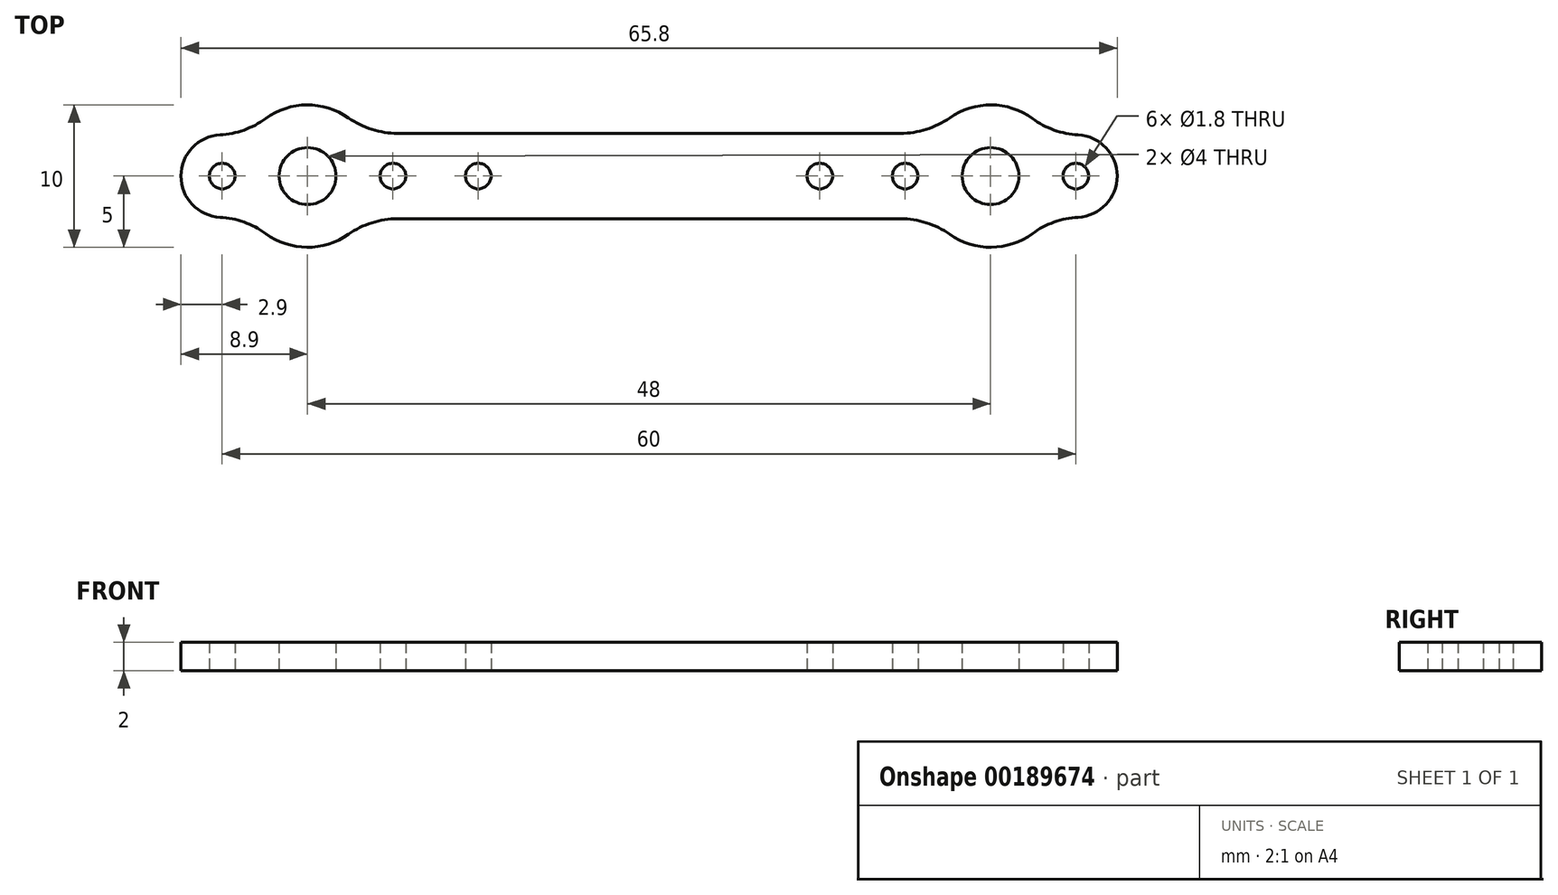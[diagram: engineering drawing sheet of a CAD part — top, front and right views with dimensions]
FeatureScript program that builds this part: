
annotation { "Feature Type Name" : "Feature", "Feature Type Description" : "" }
export const myFeature = defineFeature(function(context is Context, id is Id, definition is map)
    precondition{}
    {
        {
            var Q0;
            Q0=qCreatedBy(makeId("Top.planeOp"),FACE);
            var sketch = newSketch(context, id + "F0", { "sketchPlane" : qUnion([Q0])});
            skLineSegment(sketch, "E0", {"start": v(-24, 0) * mm, "end": v(0, 0) * mm, "construction": true});
            skCircle(sketch, "E1", {"center": v(-24, 0) * mm, "radius": 2 * mm});
            skCircle(sketch, "E2", {"center": v(-18, 0) * mm, "radius": 0.9 * mm});
            skCircle(sketch, "E3", {"center": v(-12, 0) * mm, "radius": 0.9 * mm});
            skCircle(sketch, "E4", {"center": v(-30, 0) * mm, "radius": 0.9 * mm});
            skLineSegment(sketch, "E5", {"start": v(0, 3) * mm, "end": v(-17.68, 3) * mm});
            skLineSegment(sketch, "E6.MirrorCS", {"start": v(0, -3) * mm, "end": v(-17.68, -3) * mm});
            skArc(sketch, "E7.0", {"start": v(-26.95, -4.04) * mm, "mid": v(-24.04, -5) * mm, "end": v(-21.13, -4.1) * mm});
            skArc(sketch, "E8.0", {"start": v(-30.16, 2.9) * mm, "mid": v(-32.9, 0) * mm, "end": v(-30.16, -2.9) * mm});
            skArc(sketch, "E9.trimOffspring", {"start": v(-21.13, 4.1) * mm, "mid": v(-24.04, 5) * mm, "end": v(-26.95, 4.04) * mm});
            skPoint(sketch, "E10.visualSharp", {"position": v(-20, 3) * mm});
            skArc(sketch, "E10.filletArc", {"start": v(-21.13, 4.1) * mm, "mid": v(-19.48, 3.28) * mm, "end": v(-17.68, 3) * mm});
            skPoint(sketch, "E11.visualSharp", {"position": v(-20, -3) * mm});
            skArc(sketch, "E11.filletArc", {"start": v(-17.68, -3) * mm, "mid": v(-19.48, -3.28) * mm, "end": v(-21.13, -4.1) * mm});
            skPoint(sketch, "E12.visualSharp", {"position": v(-28.38, 2.4) * mm});
            skArc(sketch, "E12.filletArc", {"start": v(-30.16, 2.9) * mm, "mid": v(-28.47, 3.23) * mm, "end": v(-26.95, 4.04) * mm});
            skPoint(sketch, "E13.visualSharp", {"position": v(-28.38, -2.4) * mm});
            skArc(sketch, "E13.filletArc", {"start": v(-26.95, -4.04) * mm, "mid": v(-28.47, -3.23) * mm, "end": v(-30.16, -2.9) * mm});
            skLineSegment(sketch, "E14", {"start": v(0, 9.05) * mm, "end": v(0, -10.47) * mm, "construction": true});
            skLineSegment(sketch, "E15.MirrorCS", {"start": v(0, 3) * mm, "end": v(17.68, 3) * mm});
            skPoint(sketch, "E16.MirrorP", {"position": v(20, 3) * mm});
            skArc(sketch, "E17.MirrorCS", {"start": v(21.13, 4.1) * mm, "mid": v(24.04, 5) * mm, "end": v(26.95, 4.04) * mm});
            skArc(sketch, "E18.MirrorCS", {"start": v(30.16, 2.9) * mm, "mid": v(28.47, 3.23) * mm, "end": v(26.95, 4.04) * mm});
            skArc(sketch, "E19.MirrorCS", {"start": v(21.13, 4.1) * mm, "mid": v(19.48, 3.28) * mm, "end": v(17.68, 3) * mm});
            skArc(sketch, "E20.MirrorCS", {"start": v(30.16, 2.9) * mm, "mid": v(32.9, 0) * mm, "end": v(30.16, -2.9) * mm});
            skArc(sketch, "E21.MirrorCS", {"start": v(26.95, -4.04) * mm, "mid": v(28.47, -3.23) * mm, "end": v(30.16, -2.9) * mm});
            skArc(sketch, "E22.MirrorCS", {"start": v(26.95, -4.04) * mm, "mid": v(24.04, -5) * mm, "end": v(21.13, -4.1) * mm});
            skArc(sketch, "E23.MirrorCS", {"start": v(17.68, -3) * mm, "mid": v(19.48, -3.28) * mm, "end": v(21.13, -4.1) * mm});
            skLineSegment(sketch, "E24.MirrorCS", {"start": v(0, -3) * mm, "end": v(17.68, -3) * mm});
            skCircle(sketch, "E25.MirrorC", {"center": v(12, 0) * mm, "radius": 0.9 * mm});
            skCircle(sketch, "E26.MirrorC", {"center": v(18, 0) * mm, "radius": 0.9 * mm});
            skCircle(sketch, "E27.MirrorC", {"center": v(24, 0) * mm, "radius": 2 * mm});
            skCircle(sketch, "E28.MirrorC", {"center": v(30, 0) * mm, "radius": 0.9 * mm});
            skSolve(sketch);
        }
        {
            var Q0;
            Q0 = qSketchRegion(id + "F0", true);
            extrude(context, id + "F1", {"entities" : qUnion([Q0]), "depth" : 2 * mm});
        }
    });
